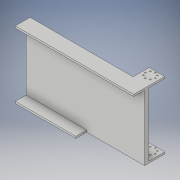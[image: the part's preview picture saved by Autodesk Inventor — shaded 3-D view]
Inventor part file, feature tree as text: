
AUTODESK INVENTOR PART (.ipt)
format: ipt  version: 2019 (Build 230136000, 136)  size: 182,272 bytes
history: native  units: in
note: dims shown in document units (in); Inventor stores cm internally (conversion verified against a paired STEP export)
features: extrude x6, sketch x6, plane x1, mirror x1
ambient origin geometry x8: Origin, YZ Plane, XZ Plane, XY Plane, X Axis, Y Axis, Z Axis, Center Point
bodies: Solid1 (feature_tree)
feature tree (14):
  extrude  "Extrusion1"  Depth=9.2in
  extrude  "Extrusion2"  Depth=0.151in
  extrude  "Extrusion3"  Depth=0.846in TaperAngle=0.0deg
  extrude  "Extrusion4"  Depth=0.151in
  extrude  "Extrusion7"  Depth=0.151in
  plane  "Work Plane1"
  mirror  "Mirror2"
  extrude  "Extrusion9"  Depth=0.151in
  sketch  "Sketch1"  dims[d0=5.223in d1=9.2in]
  sketch  "Sketch2"  dims[d2=1.15in d3=0.0in d4=0.151in]
  sketch  "Sketch3"  dims[d5=0.151in d6=0.846in d7=0.0in]
  sketch  "Sketch4"  dims[d8=4.5in d9=0.151in]
  sketch  "Sketch7"  dims[d10=0.846in d11=0.0in d12=0.151in]
  sketch  "Sketch9"  dims[d13=1.2in d14=0.151in d15=1.2in d16=1.25in d17=0.0in d39=0.2in d40=0.107in d41=0.385in d42=3.1496in d44=360.0deg d46=0.5in d47=0.0in d57=0.107in d58=0.766in d59=0.107in d60=1.5in d61=0.5in d62=0.0in]
